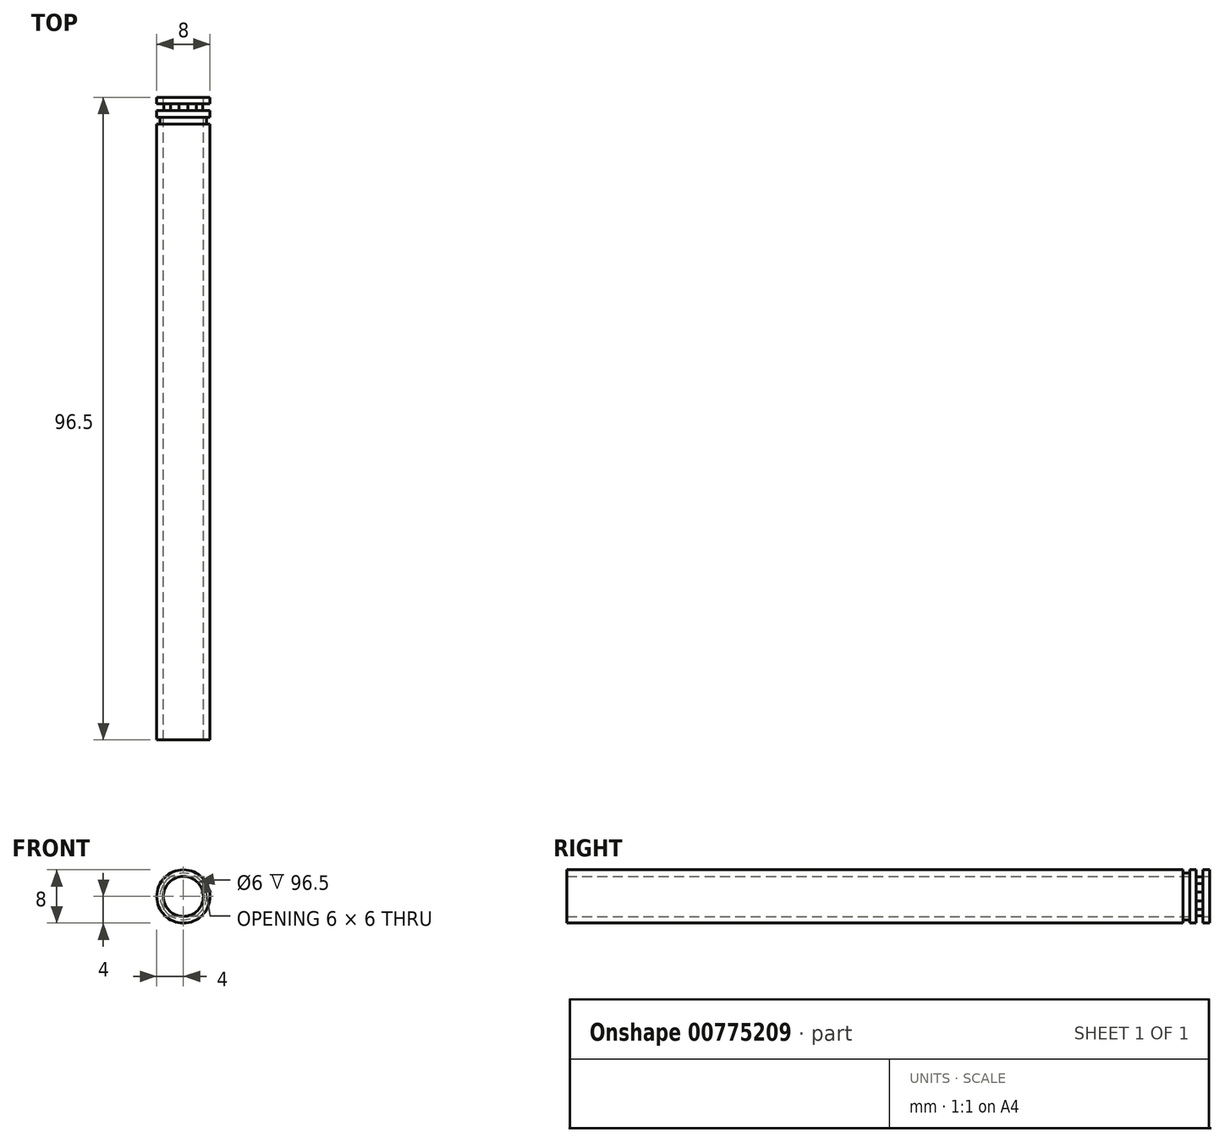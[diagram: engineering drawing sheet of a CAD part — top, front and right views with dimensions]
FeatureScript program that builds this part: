
annotation { "Feature Type Name" : "Feature", "Feature Type Description" : "" }
export const myFeature = defineFeature(function(context is Context, id is Id, definition is map)
    precondition{}
    {
        {
            var Q0;
            Q0=qCreatedBy(makeId("Front.planeOp"),FACE);
            var sketch = newSketch(context, id + "F0", { "sketchPlane" : qUnion([Q0])});
            skCircle(sketch, "E0", {"center": v(0, 0) * mm, "radius": 4 * mm});
            skCircle(sketch, "E1", {"center": v(0, 0) * mm, "radius": 3 * mm});
            skSolve(sketch);
        }
        {
            var Q0;
            Q0 = qSketchRegion(id + "F0", true);
            extrude(context, id + "F1", {"entities" : qUnion([Q0]), "depth" : 92.5 * mm, "offsetDistance" : 25 * mm});
        }
        {
            var Q0;
            Q0=makeQuery(id+"F1.opExtrude","CAP_FACE",FACE,{"disambiguationData":[OSD([sQuery(id+"F0.wireOp",EDGE,"E0"),sQuery(id+"F0.wireOp",EDGE,"E1")])],"isStart":true});
            var sketch = newSketch(context, id + "F2", { "sketchPlane" : qUnion([Q0])});
            skCircle(sketch, "E2", {"center": v(0, 0) * mm, "radius": 3 * mm});
            skCircle(sketch, "E3", {"center": v(0, 0) * mm, "radius": 3.5 * mm});
            skSolve(sketch);
        }
        {
            var Q0;
            Q0=makeQuery(id+"F2.imprint","IMPRINT",FACE,{"disambiguationData":[TD([[makeQuery(id+"F2.imprint","IMPRINT",EDGE,{"derivedFrom":sQuery(id+"F2.wireOp",EDGE,"E2")}),1.0]])]});
            extrude(context, id + "F3", {"entities" : qUnion([Q0]), "operationType" : NewBodyOperationType.ADD, "depth" : 1 * mm, "offsetDistance" : 25 * mm});
        }
        {
            var Q0;
            Q0=makeQuery(id+"F3.opExtrude","CAP_FACE",FACE,{"disambiguationData":[OSD([sQuery(id+"F2.wireOp",EDGE,"E2"),sQuery(id+"F2.wireOp",EDGE,"E3")])],"isStart":false});
            var sketch = newSketch(context, id + "F4", { "sketchPlane" : qUnion([Q0])});
            skCircle(sketch, "E4", {"center": v(0, 0) * mm, "radius": 3 * mm});
            skCircle(sketch, "E5", {"center": v(0, 0) * mm, "radius": 4 * mm});
            skSolve(sketch);
        }
        {
            var Q0;
            Q0 = qSketchRegion(id + "F4", true);
            extrude(context, id + "F5", {"entities" : qUnion([Q0]), "operationType" : NewBodyOperationType.ADD, "depth" : 1 * mm, "offsetDistance" : 25 * mm});
        }
        {
            var Q0;
            Q0=makeQuery(id+"F5.opExtrude","CAP_FACE",FACE,{"disambiguationData":[OSD([sQuery(id+"F4.wireOp",EDGE,"E4"),sQuery(id+"F4.wireOp",EDGE,"E5")])],"isStart":false});
            var sketch = newSketch(context, id + "F6", { "sketchPlane" : qUnion([Q0])});
            skCircle(sketch, "E6", {"center": v(0, 0) * mm, "radius": 3 * mm});
            skCircle(sketch, "E7", {"center": v(0, 0) * mm, "radius": 3.5 * mm});
            skSolve(sketch);
        }
        {
            var Q0;
            Q0 = qSketchRegion(id + "F6", true);
            extrude(context, id + "F7", {"entities" : qUnion([Q0]), "operationType" : NewBodyOperationType.ADD, "depth" : 1 * mm, "offsetDistance" : 25 * mm});
        }
        {
            var Q0;
            Q0=makeQuery(id+"F7.opExtrude","CAP_FACE",FACE,{"disambiguationData":[OSD([sQuery(id+"F6.wireOp",EDGE,"E6"),sQuery(id+"F6.wireOp",EDGE,"E7")])],"isStart":false});
            var sketch = newSketch(context, id + "F8", { "sketchPlane" : qUnion([Q0])});
            skLineSegment(sketch, "E8", {"start": v(-2.93, 2.92) * mm, "end": v(-2.93, -2.93) * mm});
            skLineSegment(sketch, "E9", {"start": v(-2.93, 2.92) * mm, "end": v(2.93, 2.92) * mm});
            skLineSegment(sketch, "E10", {"start": v(2.93, 2.92) * mm, "end": v(2.93, -2.93) * mm});
            skLineSegment(sketch, "E11", {"start": v(-2.93, -2.93) * mm, "end": v(2.93, -2.93) * mm});
            skLineSegment(sketch, "E12.bottom", {"start": v(-4.9, 4.81) * mm, "end": v(5.33, 4.81) * mm});
            skLineSegment(sketch, "E12.top", {"start": v(-4.9, -4.82) * mm, "end": v(5.33, -4.82) * mm});
            skLineSegment(sketch, "E12.left", {"start": v(-4.9, 4.81) * mm, "end": v(-4.9, -4.82) * mm});
            skLineSegment(sketch, "E12.right", {"start": v(5.33, 4.81) * mm, "end": v(5.33, -4.82) * mm});
            skSolve(sketch);
        }
        {
            var Q0;
            Q0 = qSketchRegion(id + "F8", true);
            extrude(context, id + "F9", {"entities" : qUnion([Q0]), "operationType" : NewBodyOperationType.REMOVE, "oppositeDirection" : true, "depth" : 1 * mm, "offsetDistance" : 25 * mm});
        }
        {
            var Q0;
            {var subQ0=sQuery(id+"F6.wireOp",EDGE,"E6");var subQ1=sQuery(id+"F6.wireOp",EDGE,"E7");Q0=makeQuery(id+"F9.boolean.opBoolean","SPLIT",FACE,{"disambiguationData":[TD([makeQuery(id+"F1.opExtrude","SWEPT_FACE",FACE,{"disambiguationData":[OSD([sQuery(id+"F0.wireOp",EDGE,"E1")])]}),makeQuery(id+"F3.opExtrude","SWEPT_FACE",FACE,{"disambiguationData":[OSD([sQuery(id+"F2.wireOp",EDGE,"E2")])]}),makeQuery(id+"F5.opExtrude","SWEPT_FACE",FACE,{"disambiguationData":[OSD([sQuery(id+"F4.wireOp",EDGE,"E4")])]}),makeQuery(id+"F7.opExtrude","SWEPT_FACE",FACE,{"disambiguationData":[OSD([subQ0])]}),makeQuery(id+"F7.opExtrude","SWEPT_FACE",FACE,{"disambiguationData":[OSD([subQ1])]}),makeQuery(id+"F9.opExtrude","SWEPT_FACE",FACE,{"disambiguationData":[OSD([sQuery(id+"F8.wireOp",EDGE,"E8")])]}),makeQuery(id+"F9.opExtrude","SWEPT_FACE",FACE,{"disambiguationData":[OSD([sQuery(id+"F8.wireOp",EDGE,"E9")])]})])],"derivedFrom":makeQuery(id+"F7.opExtrude","CAP_FACE",FACE,{"disambiguationData":[OSD([subQ0,subQ1])],"isStart":false})});}
            var sketch = newSketch(context, id + "F10", { "sketchPlane" : qUnion([Q0])});
            skCircle(sketch, "E13", {"center": v(0, 0) * mm, "radius": 3 * mm});
            skCircle(sketch, "E14", {"center": v(0, 0) * mm, "radius": 4 * mm});
            skSolve(sketch);
        }
        {
            var Q0;
            Q0 = qSketchRegion(id + "F10", true);
            extrude(context, id + "F11", {"entities" : qUnion([Q0]), "operationType" : NewBodyOperationType.ADD, "depth" : 1 * mm, "offsetDistance" : 25 * mm});
        }
    });
